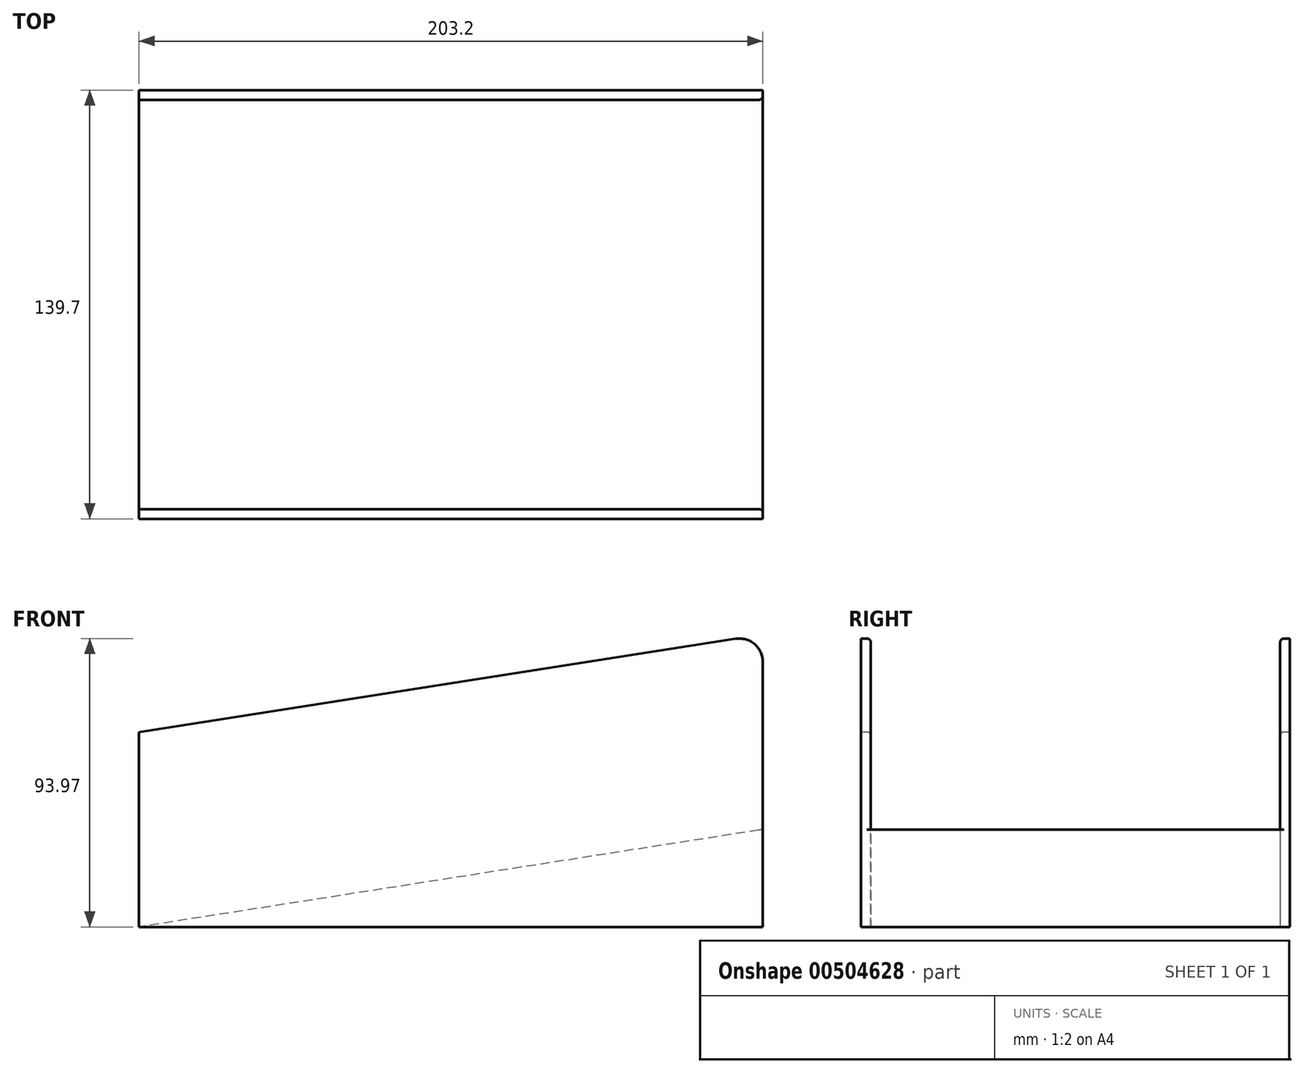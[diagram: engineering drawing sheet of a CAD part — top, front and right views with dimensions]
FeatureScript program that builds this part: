
annotation { "Feature Type Name" : "Feature", "Feature Type Description" : "" }
export const myFeature = defineFeature(function(context is Context, id is Id, definition is map)
    precondition{}
    {
        {
            var Q0;
            Q0=qCreatedBy(makeId("Top.planeOp"),FACE);
            var sketch = newSketch(context, id + "F0", { "sketchPlane" : qUnion([Q0])});
            skLineSegment(sketch, "E0.bottom", {"start": v(101.6, 66.68) * mm, "end": v(-101.6, 66.68) * mm});
            skLineSegment(sketch, "E0.top", {"start": v(101.6, -66.68) * mm, "end": v(-101.6, -66.68) * mm});
            skLineSegment(sketch, "E0.left", {"start": v(101.6, 66.67) * mm, "end": v(101.6, -66.68) * mm});
            skLineSegment(sketch, "E0.right", {"start": v(-101.6, 66.68) * mm, "end": v(-101.6, -66.68) * mm});
            skPoint(sketch, "E0.middle", {"position": v(0, 0) * mm});
            skSolve(sketch);
        }
        {
            var Q0;
            Q0=makeQuery(id+"F0.imprint","IMPRINT",FACE,{"disambiguationData":[TD([[makeQuery(id+"F0.imprint","IMPRINT",EDGE,{"derivedFrom":sQuery(id+"F0.wireOp",EDGE,"E0.bottom")}),1.0]])]});
            extrude(context, id + "F1", {"entities" : qUnion([Q0]), "depth" : 31.75 * mm});
        }
        {
            var Q0;
            Q0=makeQuery(id+"F1.opExtrude","SWEPT_FACE",FACE,{"disambiguationData":[OSD([sQuery(id+"F0.wireOp",EDGE,"E0.top")])]});
            var sketch = newSketch(context, id + "F2", { "sketchPlane" : qUnion([Q0])});
            skLineSegment(sketch, "E1", {"start": v(-101.6, 0) * mm, "end": v(101.6, 31.75) * mm});
            skLineSegment(sketch, "E2", {"start": v(101.6, 31.75) * mm, "end": v(-101.6, 31.75) * mm});
            skLineSegment(sketch, "E3", {"start": v(-101.6, 31.75) * mm, "end": v(-101.6, 0) * mm});
            skSolve(sketch);
        }
        {
            var Q0;
            Q0=makeQuery(id+"F2.imprint","IMPRINT",FACE,{"disambiguationData":[TD([[makeQuery(id+"F2.imprint","IMPRINT",EDGE,{"derivedFrom":sQuery(id+"F2.wireOp",EDGE,"E1")}),1.0]])]});
            var Q1;
            Q1=makeQuery(id+"F1.opExtrude","SWEPT_FACE",FACE,{"disambiguationData":[OSD([sQuery(id+"F0.wireOp",EDGE,"E0.bottom")])]});
            extrude(context, id + "F3", {"entities" : qUnion([Q0]), "operationType" : NewBodyOperationType.REMOVE, "endBound" : BoundingType.UP_TO_SURFACE, "oppositeDirection" : true, "endBoundEntityFace" : qUnion([Q1]), "depth" : 25.4 * mm});
        }
        {
            var Q0;
            Q0=qCreatedBy(makeId("Top.planeOp"),FACE);
            var sketch = newSketch(context, id + "F4", { "sketchPlane" : qUnion([Q0])});
            skLineSegment(sketch, "E4.bottom", {"start": v(101.6, 69.85) * mm, "end": v(-101.6, 69.85) * mm});
            skLineSegment(sketch, "E4.top", {"start": v(101.6, -69.85) * mm, "end": v(-101.6, -69.85) * mm});
            skLineSegment(sketch, "E4.left", {"start": v(101.6, 69.85) * mm, "end": v(101.6, -69.85) * mm});
            skLineSegment(sketch, "E4.right", {"start": v(-101.6, 69.85) * mm, "end": v(-101.6, -69.85) * mm});
            skPoint(sketch, "E4.middle", {"position": v(0, 0) * mm});
            skLineSegment(sketch, "E5.bottom", {"start": v(101.6, 66.67) * mm, "end": v(-101.6, 66.67) * mm});
            skLineSegment(sketch, "E5.top", {"start": v(101.6, -66.67) * mm, "end": v(-101.6, -66.67) * mm});
            skLineSegment(sketch, "E5.left", {"start": v(101.6, 66.67) * mm, "end": v(101.6, -66.67) * mm});
            skLineSegment(sketch, "E5.right", {"start": v(-101.6, 66.67) * mm, "end": v(-101.6, -66.67) * mm});
            skSolve(sketch);
        }
        {
            var Q0;
            {var subQ0=sQuery(id+"F4.wireOp",EDGE,"E4.bottom");Q0=makeQuery(id+"F4.imprint","IMPRINT",FACE,{"disambiguationData":[TD([[makeQuery(id+"F4.imprint","IMPRINT",EDGE,{"derivedFrom":subQ0}),1.0]])]});}
            var Q1;
            {var subQ0=sQuery(id+"F4.wireOp",EDGE,"E4.top");Q1=makeQuery(id+"F4.imprint","IMPRINT",FACE,{"disambiguationData":[TD([[makeQuery(id+"F4.imprint","IMPRINT",EDGE,{"derivedFrom":subQ0}),-1.0]])]});}
            extrude(context, id + "F5", {"entities" : qUnion([Q0, Q1]), "operationType" : NewBodyOperationType.ADD, "depth" : 95.25 * mm});
        }
        {
            var Q0;
            Q0=makeQuery(id+"F5.opExtrude","SWEPT_FACE",FACE,{"disambiguationData":[OSD([sQuery(id+"F4.wireOp",EDGE,"E4.top")])]});
            var sketch = newSketch(context, id + "F6", { "sketchPlane" : qUnion([Q0])});
            skLineSegment(sketch, "E6", {"start": v(101.6, 95.25) * mm, "end": v(-101.6, 63.5) * mm});
            skLineSegment(sketch, "E7", {"start": v(-101.6, 63.5) * mm, "end": v(-101.6, 95.25) * mm});
            skLineSegment(sketch, "E8", {"start": v(-101.6, 95.25) * mm, "end": v(101.6, 95.25) * mm});
            skLineSegment(sketch, "E9", {"start": v(101.6, 95.25) * mm, "end": v(101.6, 95.25) * mm});
            skSolve(sketch);
        }
        {
            var Q0;
            Q0=makeQuery(id+"F6.imprint","IMPRINT",FACE,{"disambiguationData":[TD([[makeQuery(id+"F6.imprint","IMPRINT",EDGE,{"derivedFrom":sQuery(id+"F6.wireOp",EDGE,"E6")}),-1.0]])]});
            var Q1;
            Q1=makeQuery(id+"F5.opExtrude","SWEPT_FACE",FACE,{"disambiguationData":[OSD([sQuery(id+"F4.wireOp",EDGE,"E4.bottom")])]});
            extrude(context, id + "F7", {"entities" : qUnion([Q0]), "operationType" : NewBodyOperationType.REMOVE, "endBound" : BoundingType.UP_TO_SURFACE, "oppositeDirection" : true, "endBoundEntityFace" : qUnion([Q1]), "depth" : 25.4 * mm});
        }
        {
            var Q0;
            {var subQ0=sQuery(id+"F4.wireOp",EDGE,"E4.left");var subQ1=sQuery(id+"F4.wireOp",EDGE,"E4.top");Q0=makeQuery(id+"F7.boolean.opBoolean","MERGE",EDGE,{"derivedFrom":[makeQuery(id+"F5.opExtrude","CAP_EDGE",EDGE,{"disambiguationData":[OSD([subQ0]),TDD([makeQuery(id+"F4.imprint","IMPRINT",EDGE,{"disambiguationData":[TD([[makeQuery(id+"F4.imprint","INTERSECT",VERTEX,{"derivedFrom":[subQ1,subQ0]}),1.0]])],"derivedFrom":subQ0})])],"isStart":false}),makeQuery(id+"F7.opExtrude","SWEPT_EDGE",EDGE,{"disambiguationData":[OSD([subQ1,subQ0,sQuery(id+"F6.wireOp",EDGE,"E6"),sQuery(id+"F6.wireOp",EDGE,"E8")])]})]});}
            var Q1;
            {var subQ0=sQuery(id+"F4.wireOp",EDGE,"E4.left");Q1=makeQuery(id+"F7.boolean.opBoolean","MERGE",EDGE,{"derivedFrom":[makeQuery(id+"F5.opExtrude","CAP_EDGE",EDGE,{"disambiguationData":[OSD([subQ0]),TDD([makeQuery(id+"F4.imprint","IMPRINT",EDGE,{"disambiguationData":[TD([[makeQuery(id+"F4.imprint","INTERSECT",VERTEX,{"derivedFrom":[sQuery(id+"F4.wireOp",EDGE,"E4.bottom"),subQ0]}),-1.0]])],"derivedFrom":subQ0})])],"isStart":false}),makeQuery(id+"F7.opExtrude","SWEPT_EDGE",EDGE,{"disambiguationData":[OSD([sQuery(id+"F4.wireOp",EDGE,"E4.top"),subQ0,sQuery(id+"F6.wireOp",EDGE,"E6"),sQuery(id+"F6.wireOp",EDGE,"E8")])]})]});}
            var Q2;
            {var subQ0=sQuery(id+"F4.wireOp",EDGE,"E4.right");var subQ1=sQuery(id+"F4.wireOp",EDGE,"E4.top");var subQ2=sQuery(id+"F6.wireOp",EDGE,"E6");Q2=makeQuery(id+"F7.boolean.opBoolean","COPY",EDGE,{"disambiguationData":[topologyDisambiguationEdgeConnected([makeQuery(id+"F5.opExtrude","SWEPT_FACE",FACE,{"disambiguationData":[OSD([subQ0]),TDD([makeQuery(id+"F4.imprint","IMPRINT",EDGE,{"disambiguationData":[TD([[makeQuery(id+"F4.imprint","INTERSECT",VERTEX,{"derivedFrom":[subQ1,subQ0]}),1.0]])],"derivedFrom":subQ0})])]})])],"derivedFrom":makeQuery(id+"F7.opExtrude","SWEPT_EDGE",EDGE,{"disambiguationData":[OSD([subQ1,subQ0,subQ2,sQuery(id+"F6.wireOp",EDGE,"E7")])]})});}
            var Q3;
            {var subQ0=sQuery(id+"F4.wireOp",EDGE,"E4.right");var subQ1=sQuery(id+"F6.wireOp",EDGE,"E6");Q3=makeQuery(id+"F7.boolean.opBoolean","COPY",EDGE,{"disambiguationData":[topologyDisambiguationEdgeConnected([makeQuery(id+"F5.opExtrude","SWEPT_FACE",FACE,{"disambiguationData":[OSD([subQ0]),TDD([makeQuery(id+"F4.imprint","IMPRINT",EDGE,{"disambiguationData":[TD([[makeQuery(id+"F4.imprint","INTERSECT",VERTEX,{"derivedFrom":[sQuery(id+"F4.wireOp",EDGE,"E4.bottom"),subQ0]}),-1.0]])],"derivedFrom":subQ0})])]})])],"derivedFrom":makeQuery(id+"F7.opExtrude","SWEPT_EDGE",EDGE,{"disambiguationData":[OSD([sQuery(id+"F4.wireOp",EDGE,"E4.top"),subQ0,subQ1,sQuery(id+"F6.wireOp",EDGE,"E7")])]})});}
            fillet(context, id + "F8", {"entities" : qUnion([Q0, Q1, Q2, Q3]), "radius" : 7.62 * mm, "tangentPropagation" : true, "allowEdgeOverflow" : false});
        }
        {
            var Q0;
            Q0=makeQuery(id+"F5.opExtrude","SWEPT_EDGE",EDGE,{"disambiguationData":[OSD([sQuery(id+"F4.wireOp",EDGE,"E4.left"),sQuery(id+"F4.wireOp",EDGE,"E5.top"),sQuery(id+"F4.wireOp",EDGE,"E5.left")])]});
            var Q1;
            Q1=makeQuery(id+"F5.opExtrude","SWEPT_EDGE",EDGE,{"disambiguationData":[OSD([sQuery(id+"F4.wireOp",EDGE,"E4.left"),sQuery(id+"F4.wireOp",EDGE,"E5.bottom"),sQuery(id+"F4.wireOp",EDGE,"E5.left")])]});
            fillet(context, id + "F9", {"entities" : qUnion([Q0, Q1]), "radius" : 1.27 * mm, "tangentPropagation" : true, "allowEdgeOverflow" : false});
        }
    });
